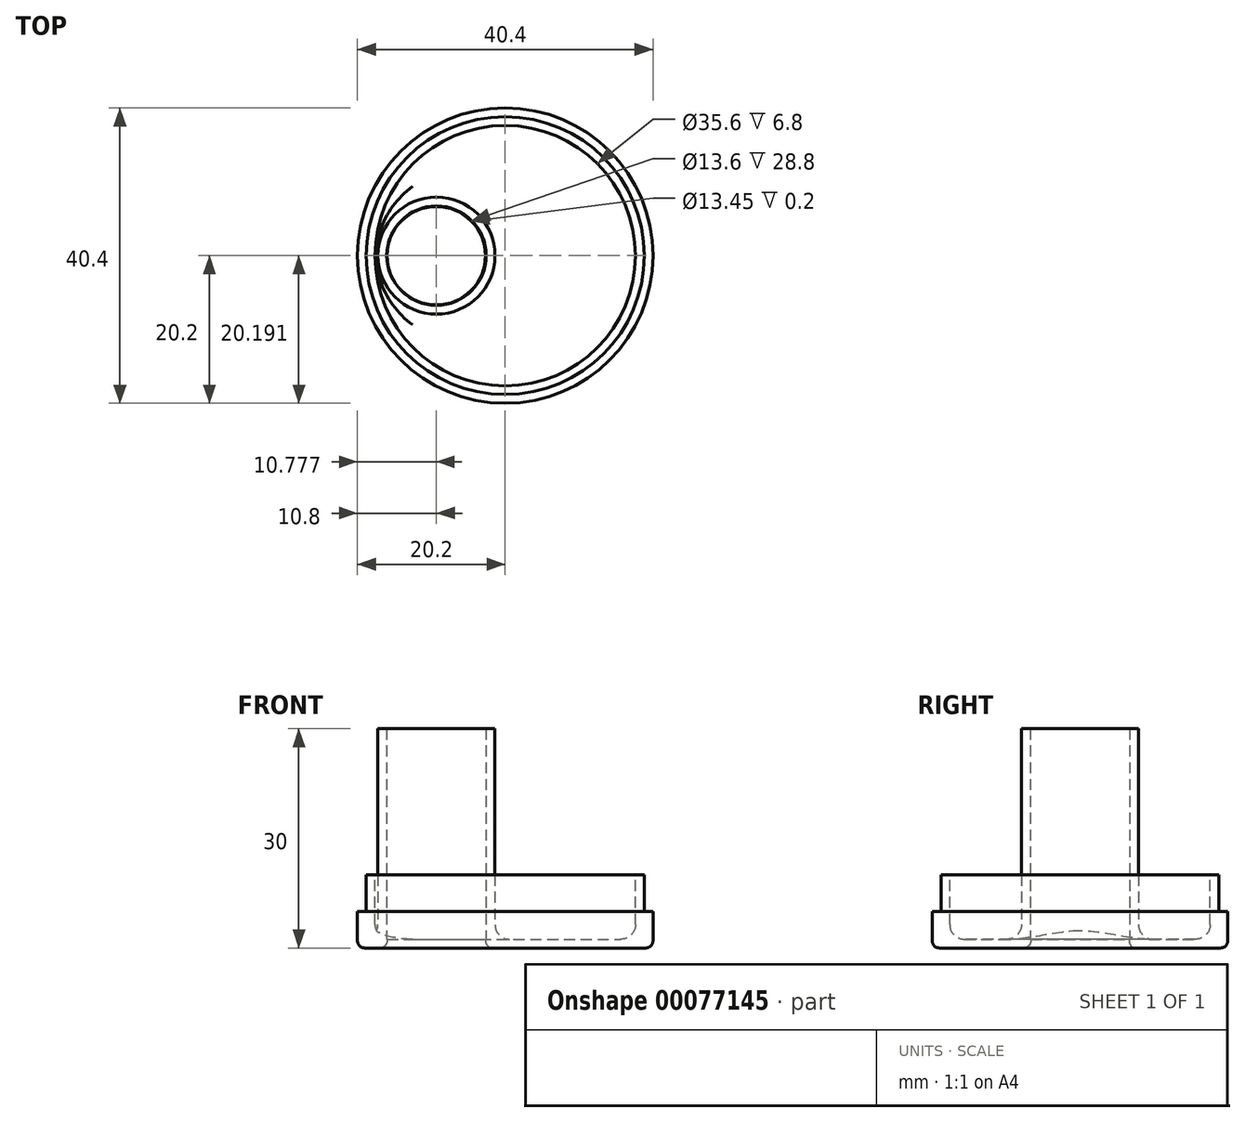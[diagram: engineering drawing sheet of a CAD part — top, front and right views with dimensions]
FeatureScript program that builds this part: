
annotation { "Feature Type Name" : "Feature", "Feature Type Description" : "" }
export const myFeature = defineFeature(function(context is Context, id is Id, definition is map)
    precondition{}
    {
        {
            var Q0;
            Q0=qCreatedBy(makeId("Front.planeOp"),FACE);
            var sketch = newSketch(context, id + "F0", { "sketchPlane" : qUnion([Q0])});
            skLineSegment(sketch, "E0", {"start": v(0, 61.92) * mm, "end": v(0, -48.9) * mm, "construction": true});
            skLineSegment(sketch, "E1", {"start": v(0, 0) * mm, "end": v(-20.2, 0) * mm});
            skLineSegment(sketch, "E2", {"start": v(-20.2, 0) * mm, "end": v(-20.2, 5) * mm});
            skLineSegment(sketch, "E3", {"start": v(-20.2, 5) * mm, "end": v(-19, 5) * mm});
            skLineSegment(sketch, "E4", {"start": v(-19, 5) * mm, "end": v(-19, 10) * mm});
            skLineSegment(sketch, "E5", {"start": v(-19, 10) * mm, "end": v(-17.8, 10) * mm});
            skLineSegment(sketch, "E6", {"start": v(-17.8, 10) * mm, "end": v(-17.8, 1.2) * mm});
            skLineSegment(sketch, "E7", {"start": v(-17.8, 1.2) * mm, "end": v(0, 1.2) * mm});
            skLineSegment(sketch, "E8", {"start": v(0, 1.2) * mm, "end": v(0, 0) * mm});
            skSolve(sketch);
        }
        {
            var Q0;
            Q0=makeQuery(id+"F0.imprint","IMPRINT",FACE,{"disambiguationData":[TD([[makeQuery(id+"F0.imprint","IMPRINT",EDGE,{"derivedFrom":sQuery(id+"F0.wireOp",EDGE,"E1")}),-1.0]])]});
            var Q1;
            Q1=sQuery(id+"F0.wireOp",EDGE,"E0");
            revolve(context, id + "F1", {"entities" : qUnion([Q0]), "axis" : qUnion([Q1]), "revolveType" : RevolveType.FULL});
        }
        {
            var Q0;
            Q0=qCreatedBy(makeId("Top.planeOp"),FACE);
            var sketch = newSketch(context, id + "F2", { "sketchPlane" : qUnion([Q0])});
            skCircle(sketch, "E9", {"center": v(-9.4, 0) * mm, "radius": 8 * mm});
            skCircle(sketch, "E10.0", {"center": v(-9.4, 0) * mm, "radius": 6.8 * mm});
            skCircle(sketch, "E11.0", {"center": v(0, 0) * mm, "radius": 22.8 * mm});
            skSolve(sketch);
        }
        {
            var Q0;
            Q0=makeQuery(id+"F2.imprint","IMPRINT",FACE,{"disambiguationData":[TD([[makeQuery(id+"F2.imprint","IMPRINT",EDGE,{"derivedFrom":sQuery(id+"F2.wireOp",EDGE,"E9")}),1.0]])]});
            extrude(context, id + "F3", {"entities" : qUnion([Q0]), "operationType" : NewBodyOperationType.ADD, "depth" : 30 * mm, "offsetDistance" : 25 * mm});
        }
        {
            var Q0;
            Q0=qCreatedBy(makeId("Top.planeOp"),FACE);
            var sketch = newSketch(context, id + "F4", { "sketchPlane" : qUnion([Q0])});
            skCircle(sketch, "E12", {"center": v(-9.42, 0) * mm, "radius": 6.72 * mm});
            skPoint(sketch, "E12.first.point", {"position": v(-12.73, -5.86) * mm});
            skPoint(sketch, "E12.second.point", {"position": v(-2.85, 1.39) * mm});
            skPoint(sketch, "E12.third.point", {"position": v(-11.7, 6.31) * mm});
            skSolve(sketch);
        }
        {
            var Q0;
            Q0=makeQuery(id+"F4.imprint","IMPRINT",FACE,{"disambiguationData":[TD([[makeQuery(id+"F4.imprint","IMPRINT",EDGE,{"derivedFrom":sQuery(id+"F4.wireOp",EDGE,"E12")}),1.0]])]});
            extrude(context, id + "F5", {"entities" : qUnion([Q0]), "operationType" : NewBodyOperationType.REMOVE, "depth" : 5 * mm, "offsetDistance" : 25 * mm, "symmetric" : true});
        }
        {
            var Q0;
            Q0=makeQuery(id+"F1.opRevolve","SWEPT_EDGE",EDGE,{"disambiguationData":[OSD([sQuery(id+"F0.wireOp",EDGE,"E1"),sQuery(id+"F0.wireOp",EDGE,"E2")])]});
            var Q1;
            Q1=makeQuery(id+"F5.boolean.opBoolean","INTERSECT",EDGE,{"derivedFrom":[makeQuery(id+"F1.opRevolve","SWEPT_FACE",FACE,{"disambiguationData":[OSD([sQuery(id+"F0.wireOp",EDGE,"E1")])]}),makeQuery(id+"F5.opExtrude","SWEPT_FACE",FACE,{"disambiguationData":[OSD([sQuery(id+"F4.wireOp",EDGE,"E12")])]})]});
            fillet(context, id + "F6", {"entities" : qUnion([Q0, Q1]), "radius" : 1 * mm, "tangentPropagation" : true, "allowEdgeOverflow" : false});
        }
        {
            var Q0;
            Q0=makeQuery(id+"F3.boolean.opBoolean","INTERSECT",EDGE,{"derivedFrom":[makeQuery(id+"F1.opRevolve","SWEPT_FACE",FACE,{"disambiguationData":[OSD([sQuery(id+"F0.wireOp",EDGE,"E7")])]}),makeQuery(id+"F3.opExtrude","SWEPT_FACE",FACE,{"disambiguationData":[OSD([sQuery(id+"F2.wireOp",EDGE,"E9")])]})]});
            var Q1;
            Q1=makeQuery(id+"F1.opRevolve","SWEPT_EDGE",EDGE,{"disambiguationData":[OSD([sQuery(id+"F0.wireOp",EDGE,"E6"),sQuery(id+"F0.wireOp",EDGE,"E7")])]});
            fillet(context, id + "F7", {"entities" : qUnion([Q0, Q1]), "radius" : 2 * mm, "tangentPropagation" : true, "allowEdgeOverflow" : false});
        }
    });
